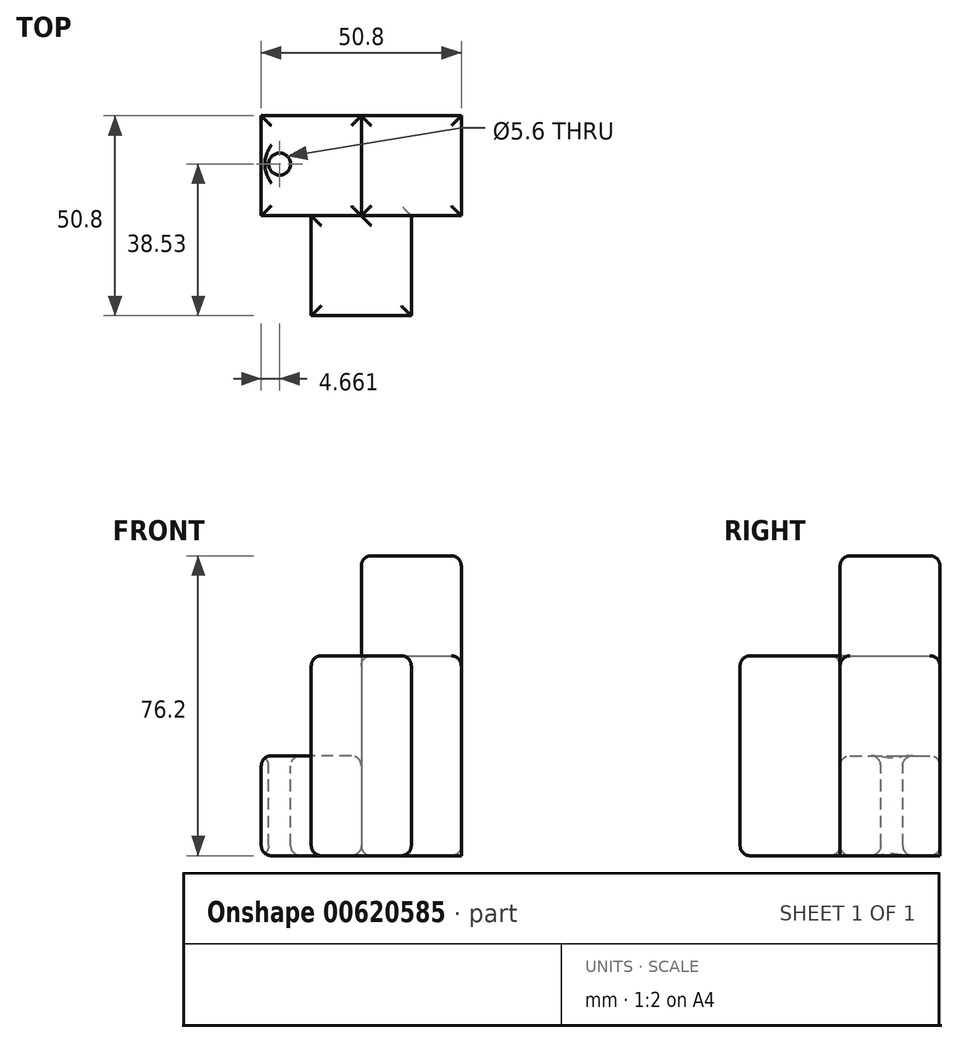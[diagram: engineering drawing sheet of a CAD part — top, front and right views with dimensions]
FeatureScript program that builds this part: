
annotation { "Feature Type Name" : "Feature", "Feature Type Description" : "" }
export const myFeature = defineFeature(function(context is Context, id is Id, definition is map)
    precondition{}
    {
        {
            var Q0;
            Q0=qCreatedBy(makeId("Top.planeOp"),FACE);
            var sketch = newSketch(context, id + "F0", { "sketchPlane" : qUnion([Q0])});
            skLineSegment(sketch, "E0.bottom", {"start": v(0, 0) * mm, "end": v(-25.4, 0) * mm});
            skLineSegment(sketch, "E0.top", {"start": v(0, 25.4) * mm, "end": v(-25.4, 25.4) * mm});
            skLineSegment(sketch, "E0.left", {"start": v(0, 0) * mm, "end": v(0, 25.4) * mm});
            skLineSegment(sketch, "E0.right", {"start": v(-25.4, 0) * mm, "end": v(-25.4, 25.4) * mm});
            skLineSegment(sketch, "E1.bottom", {"start": v(0, 25.4) * mm, "end": v(25.4, 25.4) * mm});
            skLineSegment(sketch, "E1.top", {"start": v(0, 0) * mm, "end": v(25.4, 0) * mm});
            skLineSegment(sketch, "E1.left", {"start": v(0, 25.4) * mm, "end": v(0, 0) * mm});
            skLineSegment(sketch, "E1.right", {"start": v(25.4, 25.4) * mm, "end": v(25.4, 0) * mm});
            skLineSegment(sketch, "E2.bottom", {"start": v(-12.7, 0) * mm, "end": v(12.7, 0) * mm});
            skLineSegment(sketch, "E2.top", {"start": v(-12.7, -25.4) * mm, "end": v(12.7, -25.4) * mm});
            skLineSegment(sketch, "E2.left", {"start": v(-12.7, 0) * mm, "end": v(-12.7, -25.4) * mm});
            skLineSegment(sketch, "E2.right", {"start": v(12.7, 0) * mm, "end": v(12.7, -25.4) * mm});
            skSolve(sketch);
        }
        {
            var Q0;
            {var subQ1=sQuery(id+"F0.wireOp",EDGE,"E0.bottom");Q0=makeQuery(id+"F0.imprint","IMPRINT",FACE,{"disambiguationData":[TD([[makeQuery(id+"F0.imprint","IMPRINT",EDGE,{"derivedFrom":subQ1}),-1.0]])]});}
            extrude(context, id + "F1", {"entities" : qUnion([Q0]), "depth" : 25.4 * mm, "offsetDistance" : 25.4 * mm});
        }
        {
            var Q0;
            Q0=qCreatedBy(makeId("Top.planeOp"),FACE);
            var sketch = newSketch(context, id + "F2", { "sketchPlane" : qUnion([Q0])});
            skLineSegment(sketch, "E3.bottom", {"start": v(0, 0) * mm, "end": v(25.4, 0) * mm});
            skLineSegment(sketch, "E3.top", {"start": v(0, 25.4) * mm, "end": v(25.4, 25.4) * mm});
            skLineSegment(sketch, "E3.left", {"start": v(0, 0) * mm, "end": v(0, 25.4) * mm});
            skLineSegment(sketch, "E3.right", {"start": v(25.4, 0) * mm, "end": v(25.4, 25.4) * mm});
            skLineSegment(sketch, "E4.bottom", {"start": v(12.7, 0) * mm, "end": v(-12.7, 0) * mm});
            skLineSegment(sketch, "E4.top", {"start": v(12.7, -25.4) * mm, "end": v(-12.7, -25.4) * mm});
            skLineSegment(sketch, "E4.left", {"start": v(12.7, 0) * mm, "end": v(12.7, -25.4) * mm});
            skLineSegment(sketch, "E4.right", {"start": v(-12.7, 0) * mm, "end": v(-12.7, -25.4) * mm});
            skSolve(sketch);
        }
        {
            var Q0;
            {var subQ1=sQuery(id+"F2.wireOp",EDGE,"E3.bottom");Q0=makeQuery(id+"F2.imprint","IMPRINT",FACE,{"disambiguationData":[TD([[makeQuery(id+"F2.imprint","IMPRINT",EDGE,{"derivedFrom":subQ1}),1.0]])]});}
            extrude(context, id + "F3", {"entities" : qUnion([Q0]), "depth" : 76.2 * mm, "offsetDistance" : 25.4 * mm});
        }
        {
            var Q0;
            Q0 = qSketchRegion(id + "F2", true);
            extrude(context, id + "F4", {"entities" : qUnion([Q0]), "depth" : 50.8 * mm, "offsetDistance" : 25.4 * mm});
        }
        {
            var Q0;
            Q0=makeQuery(id+"F1.opExtrude","CAP_FACE",FACE,{"disambiguationData":[OSD([sQuery(id+"F0.wireOp",EDGE,"E0.bottom"),sQuery(id+"F0.wireOp",EDGE,"E0.top"),sQuery(id+"F0.wireOp",EDGE,"E0.right"),sQuery(id+"F0.wireOp",EDGE,"E1.left"),sQuery(id+"F0.wireOp",EDGE,"E2.bottom")])],"isStart":false});
            var sketch = newSketch(context, id + "F5", { "sketchPlane" : qUnion([Q0])});
            skCircle(sketch, "E5", {"center": v(-20.74, 13.13) * mm, "radius": 2.8 * mm});
            skSolve(sketch);
        }
        {
            var Q0;
            Q0 = qSketchRegion(id + "F5", true);
            extrude(context, id + "F6", {"entities" : qUnion([Q0]), "operationType" : NewBodyOperationType.REMOVE, "oppositeDirection" : true, "depth" : 40.64 * mm, "offsetDistance" : 25.4 * mm});
        }
        {
            var Q0;
            Q0=makeQuery(id+"F3.opExtrude","CAP_FACE",FACE,{"disambiguationData":[OSD([sQuery(id+"F2.wireOp",EDGE,"E3.bottom"),sQuery(id+"F2.wireOp",EDGE,"E3.top"),sQuery(id+"F2.wireOp",EDGE,"E3.left"),sQuery(id+"F2.wireOp",EDGE,"E3.right"),sQuery(id+"F2.wireOp",EDGE,"E4.bottom")])],"isStart":false});
            var Q1;
            Q1=makeQuery(id+"F4.opExtrude","CAP_FACE",FACE,{"disambiguationData":[OSD([sQuery(id+"F2.wireOp",EDGE,"E3.bottom"),sQuery(id+"F2.wireOp",EDGE,"E3.top"),sQuery(id+"F2.wireOp",EDGE,"E3.left"),sQuery(id+"F2.wireOp",EDGE,"E3.right"),sQuery(id+"F2.wireOp",EDGE,"E4.bottom"),sQuery(id+"F2.wireOp",EDGE,"E4.top"),sQuery(id+"F2.wireOp",EDGE,"E4.left"),sQuery(id+"F2.wireOp",EDGE,"E4.right")])],"isStart":false});
            var Q2;
            Q2=makeQuery(id+"F1.opExtrude","CAP_FACE",FACE,{"disambiguationData":[OSD([sQuery(id+"F0.wireOp",EDGE,"E0.bottom"),sQuery(id+"F0.wireOp",EDGE,"E0.top"),sQuery(id+"F0.wireOp",EDGE,"E0.right"),sQuery(id+"F0.wireOp",EDGE,"E1.left"),sQuery(id+"F0.wireOp",EDGE,"E2.bottom")])],"isStart":false});
            var Q3;
            Q3=makeQuery(id+"F4.opExtrude","CAP_FACE",FACE,{"disambiguationData":[OSD([sQuery(id+"F2.wireOp",EDGE,"E3.bottom"),sQuery(id+"F2.wireOp",EDGE,"E3.top"),sQuery(id+"F2.wireOp",EDGE,"E3.left"),sQuery(id+"F2.wireOp",EDGE,"E3.right"),sQuery(id+"F2.wireOp",EDGE,"E4.bottom"),sQuery(id+"F2.wireOp",EDGE,"E4.top"),sQuery(id+"F2.wireOp",EDGE,"E4.left"),sQuery(id+"F2.wireOp",EDGE,"E4.right")])],"isStart":true});
            var Q4;
            Q4=makeQuery(id+"F1.opExtrude","CAP_FACE",FACE,{"disambiguationData":[OSD([sQuery(id+"F0.wireOp",EDGE,"E0.bottom"),sQuery(id+"F0.wireOp",EDGE,"E0.top"),sQuery(id+"F0.wireOp",EDGE,"E0.right"),sQuery(id+"F0.wireOp",EDGE,"E1.left"),sQuery(id+"F0.wireOp",EDGE,"E2.bottom")])],"isStart":true});
            fillet(context, id + "F7", {"entities" : qUnion([Q0, Q1, Q2, Q3, Q4]), "radius" : 2.54 * mm, "tangentPropagation" : true, "allowEdgeOverflow" : false});
        }
    });
